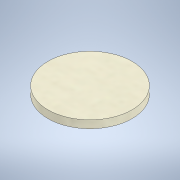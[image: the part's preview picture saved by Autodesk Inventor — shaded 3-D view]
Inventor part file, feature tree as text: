
AUTODESK INVENTOR PART (.ipt)
format: ipt  version: 2021 (Build 250183000, 183)  size: 101,888 bytes
history: native  units: mm
features: extrude x1, sketch x1
ambient origin geometry x8: Origin, YZ Plane, XZ Plane, XY Plane, X Axis, Y Axis, Z Axis, Center Point
bodies: Solid1 (feature_tree)
feature tree (2):
  extrude  "Extrusion1"  Depth=3.45mm TaperAngle=0.0deg
  sketch  "Sketch1"  dims[d0=37.8mm d1=3.45mm d2=0.0mm]
